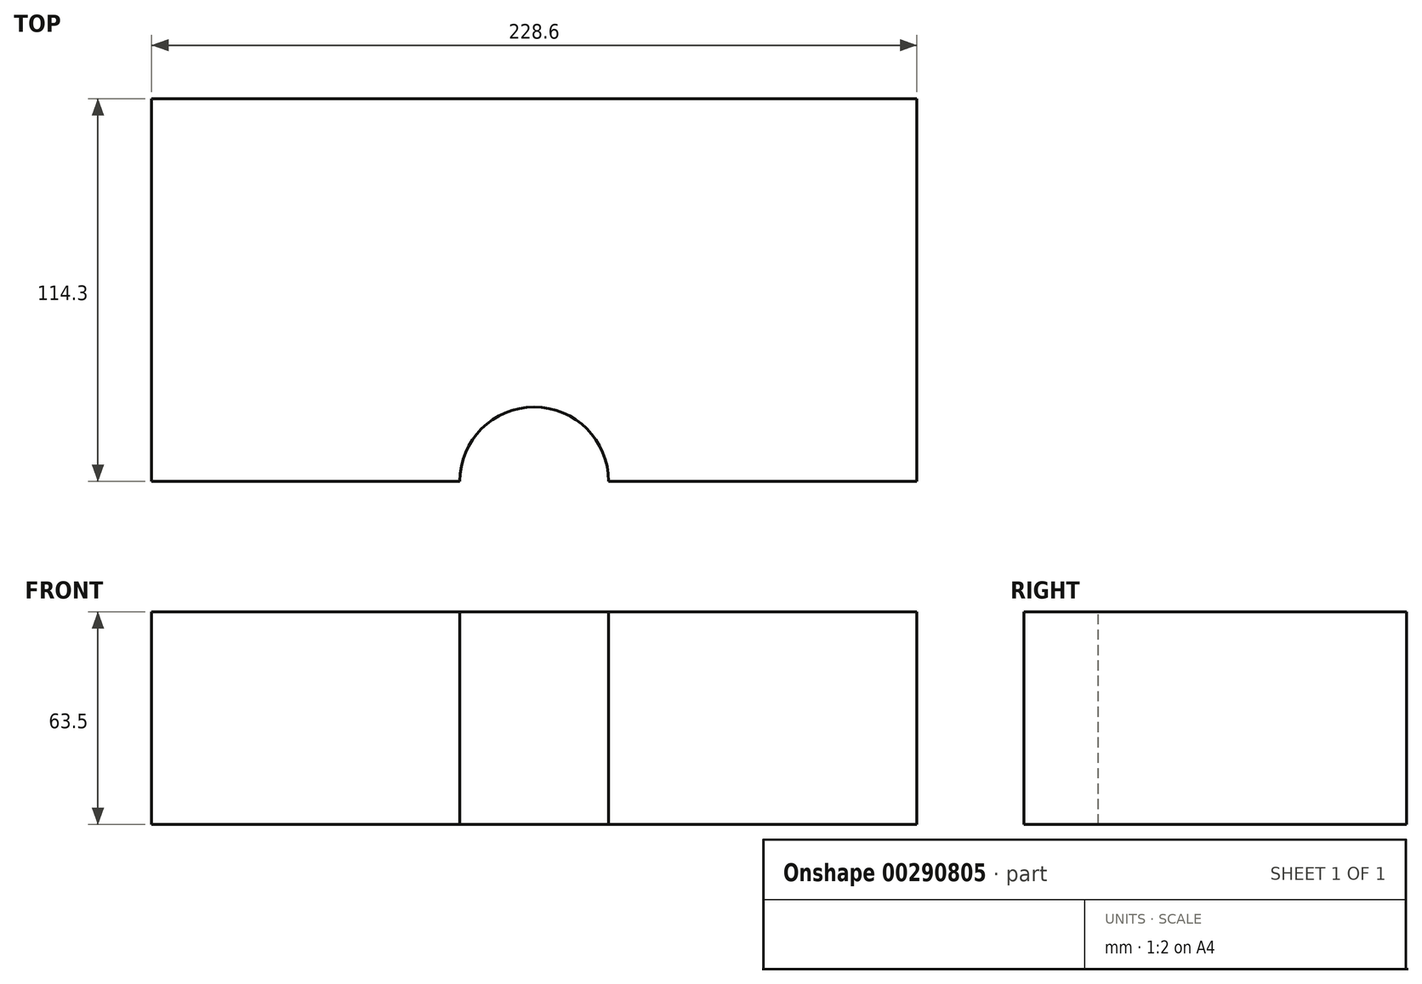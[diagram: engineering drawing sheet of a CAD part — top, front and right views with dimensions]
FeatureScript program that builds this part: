
annotation { "Feature Type Name" : "Feature", "Feature Type Description" : "" }
export const myFeature = defineFeature(function(context is Context, id is Id, definition is map)
    precondition{}
    {
        {
            var Q0;
            Q0=qCreatedBy(makeId("Top.planeOp"),FACE);
            var sketch = newSketch(context, id + "F0", { "sketchPlane" : qUnion([Q0])});
            skLineSegment(sketch, "E0.bottom", {"start": v(-114.3, 114.3) * mm, "end": v(114.3, 114.3) * mm});
            skLineSegment(sketch, "E0.top", {"start": v(-114.3, 0) * mm, "end": v(-22.23, 0) * mm});
            skLineSegment(sketch, "E0.left", {"start": v(-114.3, 114.3) * mm, "end": v(-114.3, 0) * mm});
            skLineSegment(sketch, "E0.right", {"start": v(114.3, 114.3) * mm, "end": v(114.3, 0) * mm});
            skArc(sketch, "E1", {"start": v(22.23, 0) * mm, "mid": v(0, 22.23) * mm, "end": v(-22.23, 0) * mm});
            skLineSegment(sketch, "E2.trimOffspring", {"start": v(22.23, 0) * mm, "end": v(114.3, 0) * mm});
            skSolve(sketch);
        }
        {
            var Q0;
            Q0 = qSketchRegion(id + "F0", true);
            extrude(context, id + "F1", {"entities" : qUnion([Q0]), "oppositeDirection" : true, "depth" : 63.5 * mm});
        }
    });
